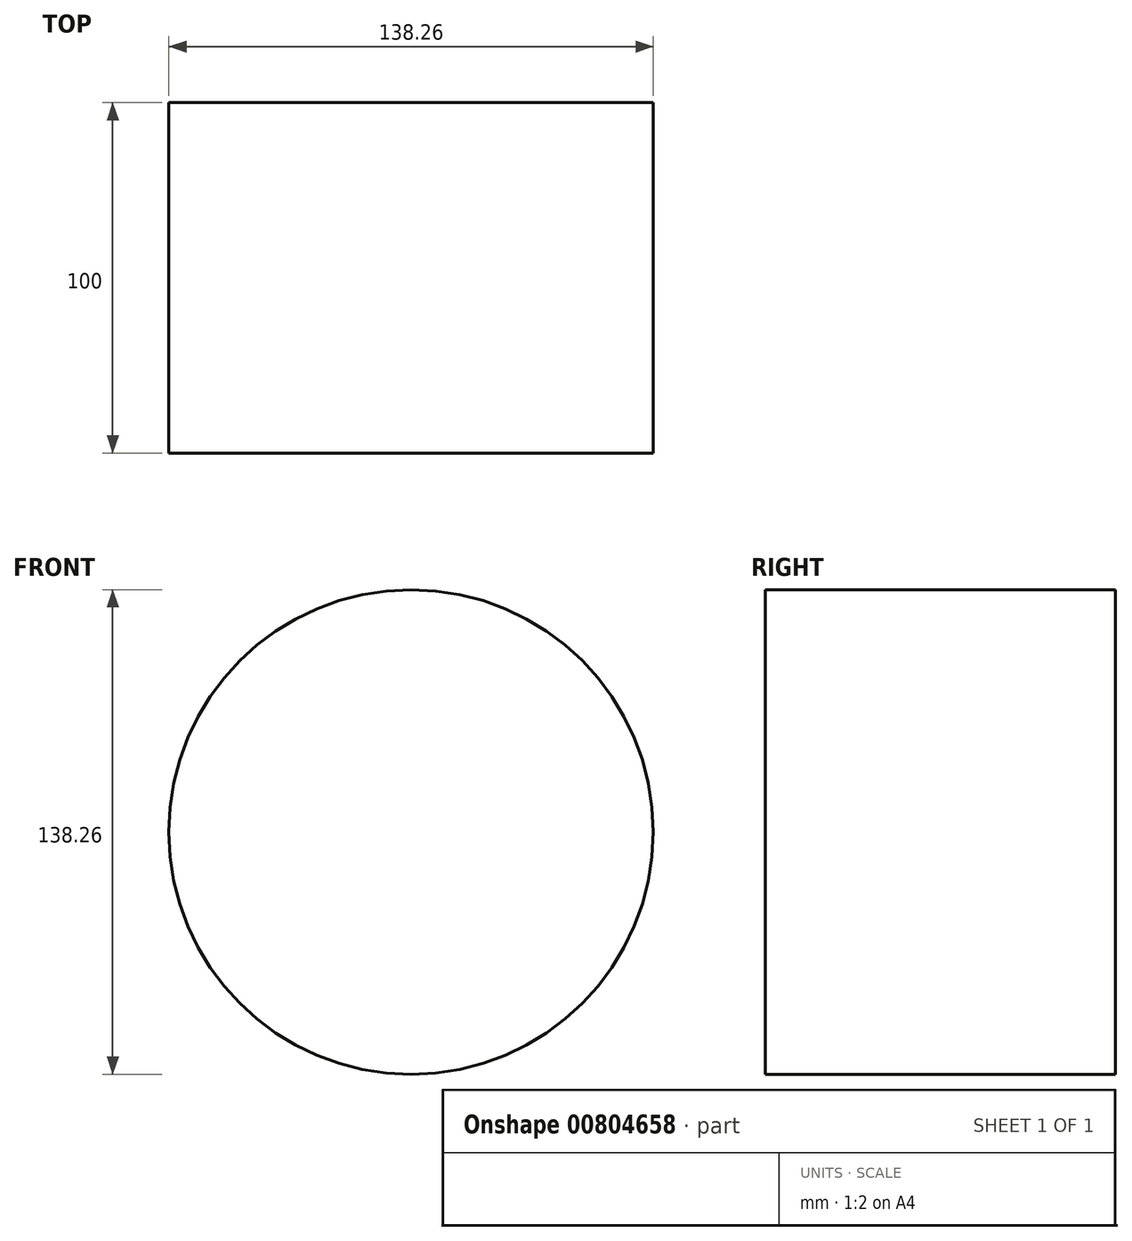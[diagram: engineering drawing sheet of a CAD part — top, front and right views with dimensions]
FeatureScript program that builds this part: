
annotation { "Feature Type Name" : "Feature", "Feature Type Description" : "" }
export const myFeature = defineFeature(function(context is Context, id is Id, definition is map)
    precondition{}
    {
        {
            var Q0;
            Q0=qCreatedBy(makeId("Front.planeOp"),FACE);
            var sketch = newSketch(context, id + "F0", { "sketchPlane" : qUnion([Q0])});
            skCircle(sketch, "E0", {"center": v(0, 0) * mm, "radius": 69.13 * mm});
            skSolve(sketch);
        }
        {
            var Q0;
            Q0=makeQuery(id+"F0.imprint","IMPRINT",FACE,{"disambiguationData":[TD([[makeQuery(id+"F0.imprint","IMPRINT",EDGE,{"derivedFrom":sQuery(id+"F0.wireOp",EDGE,"E0")}),1.0]])]});
            extrude(context, id + "F1", {"entities" : qUnion([Q0]), "depth" : 100 * mm, "offsetDistance" : 25 * mm});
        }
    });
